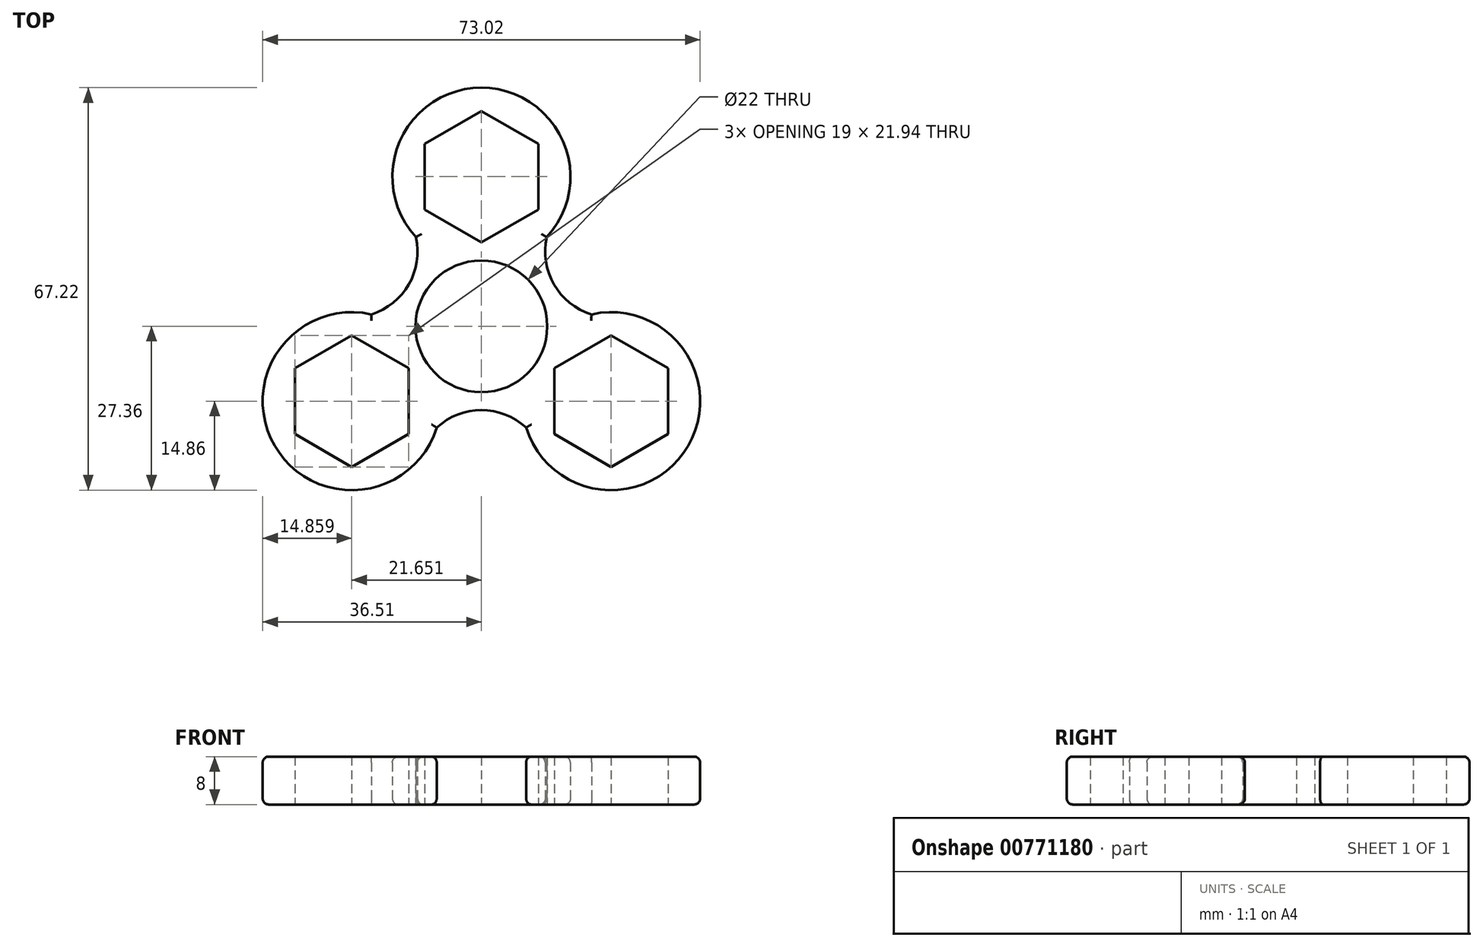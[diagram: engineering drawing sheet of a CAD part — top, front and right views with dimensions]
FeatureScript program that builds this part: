
annotation { "Feature Type Name" : "Feature", "Feature Type Description" : "" }
export const myFeature = defineFeature(function(context is Context, id is Id, definition is map)
    precondition{}
    {
        {
            var Q0;
            Q0=qCreatedBy(makeId("Top.planeOp"),FACE);
            var sketch = newSketch(context, id + "F0", { "sketchPlane" : qUnion([Q0])});
            skCircle(sketch, "E0", {"center": v(0, 0) * mm, "radius": 11 * mm});
            skLineSegment(sketch, "E1", {"start": v(-74.79, 0) * mm, "end": v(74.79, 0) * mm, "construction": true});
            skLineSegment(sketch, "E2", {"start": v(0, 61.61) * mm, "end": v(0, -14) * mm, "construction": true});
            skArc(sketch, "E3", {"start": v(7.46, -16.92) * mm, "mid": v(0, -14) * mm, "end": v(-7.46, -16.92) * mm});
            skArc(sketch, "E4.1.0", {"start": v(10.92, 14.92) * mm, "mid": v(12.12, 7) * mm, "end": v(18.38, 2) * mm});
            skArc(sketch, "E4.2.0", {"start": v(-18.38, 2) * mm, "mid": v(-12.12, 7) * mm, "end": v(-10.92, 14.92) * mm});
            skLineSegment(sketch, "E5.trimOffspring", {"start": v(0, -25) * mm, "end": v(0, -57.25) * mm});
            skArc(sketch, "E6", {"start": v(10.92, 14.92) * mm, "mid": v(0, 39.86) * mm, "end": v(-10.92, 14.92) * mm});
            skArc(sketch, "E7", {"start": v(-18.38, 2) * mm, "mid": v(-34.52, -19.93) * mm, "end": v(-7.46, -16.92) * mm});
            skArc(sketch, "E8", {"start": v(7.46, -16.92) * mm, "mid": v(34.52, -19.93) * mm, "end": v(18.38, 2) * mm});
            skCircle(sketch, "E9.cCircle", {"center": v(0, 25) * mm, "radius": 9.5 * mm, "construction": true});
            skLineSegment(sketch, "E9.0", {"start": v(9.5, 30.48) * mm, "end": v(9.5, 19.52) * mm});
            skLineSegment(sketch, "E9.1", {"start": v(9.5, 19.52) * mm, "end": v(0, 14.03) * mm});
            skLineSegment(sketch, "E9.2", {"start": v(0, 14.03) * mm, "end": v(-9.5, 19.52) * mm});
            skLineSegment(sketch, "E9.3", {"start": v(-9.5, 19.52) * mm, "end": v(-9.5, 30.48) * mm});
            skLineSegment(sketch, "E9.4", {"start": v(-9.5, 30.48) * mm, "end": v(0, 35.97) * mm});
            skLineSegment(sketch, "E9.5", {"start": v(0, 35.97) * mm, "end": v(9.5, 30.48) * mm});
            skPoint(sketch, "E9.0.midPoint", {"position": v(9.5, 25) * mm});
            skLineSegment(sketch, "E10.1.0", {"start": v(-21.65, -23.47) * mm, "end": v(-31.15, -17.98) * mm});
            skLineSegment(sketch, "E10.1.1", {"start": v(-12.15, -17.98) * mm, "end": v(-21.65, -23.47) * mm});
            skLineSegment(sketch, "E10.1.2", {"start": v(-12.15, -7.02) * mm, "end": v(-12.15, -17.98) * mm});
            skLineSegment(sketch, "E10.1.3", {"start": v(-21.65, -1.53) * mm, "end": v(-12.15, -7.02) * mm});
            skLineSegment(sketch, "E10.1.4", {"start": v(-31.15, -7.02) * mm, "end": v(-21.65, -1.53) * mm});
            skLineSegment(sketch, "E10.1.5", {"start": v(-31.15, -17.98) * mm, "end": v(-31.15, -7.02) * mm});
            skLineSegment(sketch, "E10.2.0", {"start": v(31.15, -7.02) * mm, "end": v(31.15, -17.98) * mm});
            skLineSegment(sketch, "E10.2.1", {"start": v(21.65, -1.53) * mm, "end": v(31.15, -7.02) * mm});
            skLineSegment(sketch, "E10.2.2", {"start": v(12.15, -7.02) * mm, "end": v(21.65, -1.53) * mm});
            skLineSegment(sketch, "E10.2.3", {"start": v(12.15, -17.98) * mm, "end": v(12.15, -7.02) * mm});
            skLineSegment(sketch, "E10.2.4", {"start": v(21.65, -23.47) * mm, "end": v(12.15, -17.98) * mm});
            skLineSegment(sketch, "E10.2.5", {"start": v(31.15, -17.98) * mm, "end": v(21.65, -23.47) * mm});
            skSolve(sketch);
        }
        {
            var Q0;
            Q0=makeQuery(id+"F0.imprint","IMPRINT",FACE,{"disambiguationData":[TD([[makeQuery(id+"F0.imprint","IMPRINT",EDGE,{"derivedFrom":sQuery(id+"F0.wireOp",EDGE,"E0")}),-1.0]])]});
            extrude(context, id + "F1", {"entities" : qUnion([Q0]), "depth" : 8 * mm, "offsetDistance" : 25 * mm});
        }
        {
            var Q0;
            Q0=makeQuery(id+"F1.opExtrude","CAP_EDGE",EDGE,{"disambiguationData":[OSD([sQuery(id+"F0.wireOp",EDGE,"E7")])],"isStart":false});
            var Q1;
            Q1=makeQuery(id+"F1.opExtrude","CAP_EDGE",EDGE,{"disambiguationData":[OSD([sQuery(id+"F0.wireOp",EDGE,"E8")])],"isStart":false});
            var Q2;
            Q2=makeQuery(id+"F1.opExtrude","CAP_EDGE",EDGE,{"disambiguationData":[OSD([sQuery(id+"F0.wireOp",EDGE,"E3")])],"isStart":false});
            var Q3;
            Q3=makeQuery(id+"F1.opExtrude","CAP_EDGE",EDGE,{"disambiguationData":[OSD([sQuery(id+"F0.wireOp",EDGE,"E4.1.0")])],"isStart":false});
            var Q4;
            Q4=makeQuery(id+"F1.opExtrude","CAP_EDGE",EDGE,{"disambiguationData":[OSD([sQuery(id+"F0.wireOp",EDGE,"E4.2.0")])],"isStart":false});
            var Q5;
            Q5=makeQuery(id+"F1.opExtrude","CAP_EDGE",EDGE,{"disambiguationData":[OSD([sQuery(id+"F0.wireOp",EDGE,"E6")])],"isStart":false});
            fillet(context, id + "F2", {"entities" : qUnion([Q0, Q1, Q2, Q3, Q4, Q5]), "radius" : 1 * mm, "tangentPropagation" : true, "allowEdgeOverflow" : false});
        }
        {
            var Q0;
            Q0=makeQuery(id+"F1.opExtrude","CAP_EDGE",EDGE,{"disambiguationData":[OSD([sQuery(id+"F0.wireOp",EDGE,"E4.2.0")])],"isStart":true});
            var Q1;
            Q1=makeQuery(id+"F1.opExtrude","CAP_EDGE",EDGE,{"disambiguationData":[OSD([sQuery(id+"F0.wireOp",EDGE,"E6")])],"isStart":true});
            var Q2;
            Q2=makeQuery(id+"F1.opExtrude","CAP_EDGE",EDGE,{"disambiguationData":[OSD([sQuery(id+"F0.wireOp",EDGE,"E7")])],"isStart":true});
            var Q3;
            Q3=makeQuery(id+"F1.opExtrude","CAP_EDGE",EDGE,{"disambiguationData":[OSD([sQuery(id+"F0.wireOp",EDGE,"E3")])],"isStart":true});
            var Q4;
            Q4=makeQuery(id+"F1.opExtrude","CAP_EDGE",EDGE,{"disambiguationData":[OSD([sQuery(id+"F0.wireOp",EDGE,"E4.1.0")])],"isStart":true});
            var Q5;
            Q5=makeQuery(id+"F1.opExtrude","CAP_EDGE",EDGE,{"disambiguationData":[OSD([sQuery(id+"F0.wireOp",EDGE,"E8")])],"isStart":true});
            fillet(context, id + "F3", {"entities" : qUnion([Q0, Q1, Q2, Q3, Q4, Q5]), "radius" : 1 * mm, "tangentPropagation" : true, "allowEdgeOverflow" : false});
        }
    });
